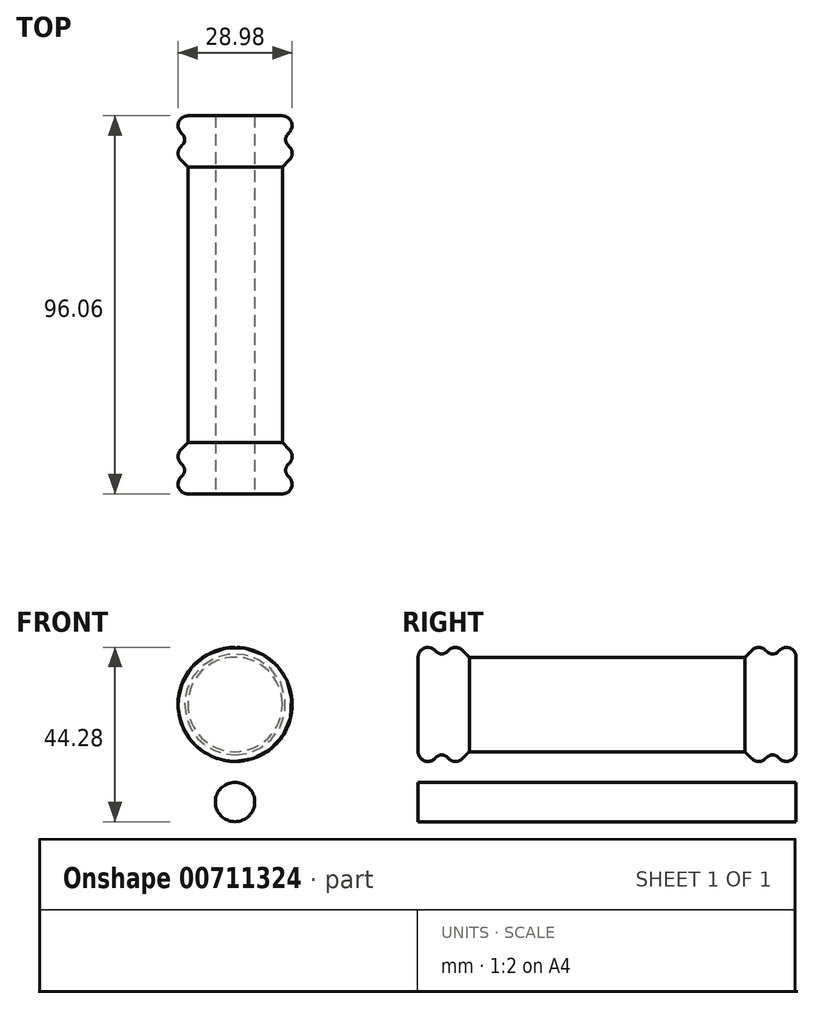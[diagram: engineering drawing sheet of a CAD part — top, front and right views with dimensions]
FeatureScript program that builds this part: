
annotation { "Feature Type Name" : "Feature", "Feature Type Description" : "" }
export const myFeature = defineFeature(function(context is Context, id is Id, definition is map)
    precondition{}
    {
        {
            var Q0;
            Q0=qCreatedBy(makeId("Right.planeOp"),FACE);
            var sketch = newSketch(context, id + "F0", { "sketchPlane" : qUnion([Q0])});
            skLineSegment(sketch, "E0", {"start": v(-48.03, 0) * mm, "end": v(-48.03, 12) * mm});
            skLineSegment(sketch, "E1", {"start": v(-43.79, 13.76) * mm, "end": v(-42.03, 12) * mm});
            skLineSegment(sketch, "E2", {"start": v(-42.03, 12) * mm, "end": v(-40.27, 13.76) * mm});
            skLineSegment(sketch, "E3", {"start": v(-36.76, 13.76) * mm, "end": v(-35, 12) * mm});
            skLineSegment(sketch, "E4", {"start": v(-48.03, 0) * mm, "end": v(48.03, 0) * mm});
            skLineSegment(sketch, "E5", {"start": v(-35, 12) * mm, "end": v(35, 12) * mm});
            skArc(sketch, "E6", {"start": v(-43.79, 13.76) * mm, "mid": v(-46.5, 14.3) * mm, "end": v(-48.03, 12) * mm});
            skArc(sketch, "E7", {"start": v(-36.76, 13.76) * mm, "mid": v(-38.51, 14.49) * mm, "end": v(-40.27, 13.76) * mm});
            skArc(sketch, "E8.MirrorCS", {"start": v(36.76, 13.76) * mm, "mid": v(38.51, 14.49) * mm, "end": v(40.27, 13.76) * mm});
            skLineSegment(sketch, "E9.MirrorCS", {"start": v(36.76, 13.76) * mm, "end": v(35, 12) * mm});
            skLineSegment(sketch, "E10.MirrorCS", {"start": v(42.03, 12) * mm, "end": v(40.27, 13.76) * mm});
            skLineSegment(sketch, "E11.MirrorCS", {"start": v(48.03, 0) * mm, "end": v(48.03, 12) * mm});
            skLineSegment(sketch, "E12.MirrorCS", {"start": v(43.79, 13.76) * mm, "end": v(42.03, 12) * mm});
            skArc(sketch, "E13.MirrorCS", {"start": v(43.79, 13.76) * mm, "mid": v(46.5, 14.3) * mm, "end": v(48.03, 12) * mm});
            skLineSegment(sketch, "E14.bottom", {"start": v(-48.03, -19.79) * mm, "end": v(48.03, -19.79) * mm});
            skLineSegment(sketch, "E14.top", {"start": v(-48.03, -24.79) * mm, "end": v(48.03, -24.79) * mm});
            skLineSegment(sketch, "E14.left", {"start": v(-48.03, -19.79) * mm, "end": v(-48.03, -24.79) * mm});
            skLineSegment(sketch, "E14.right", {"start": v(48.03, -19.79) * mm, "end": v(48.03, -24.79) * mm});
            skSolve(sketch);
        }
        {
            var Q0;
            Q0=makeQuery(id+"F0.imprint","IMPRINT",FACE,{"disambiguationData":[TD([[makeQuery(id+"F0.imprint","IMPRINT",EDGE,{"derivedFrom":sQuery(id+"F0.wireOp",EDGE,"E0")}),-1.0]])]});
            var Q1;
            Q1=sQuery(id+"F0.wireOp",EDGE,"E4");
            revolve(context, id + "F1", {"surfaceOperationType" : NewSurfaceOperationType.NEW, "entities" : qUnion([Q0]), "axis" : qUnion([Q1]), "revolveType" : RevolveType.FULL});
        }
        {
            var Q0;
            Q0=makeQuery(id+"F1.opRevolve","SWEPT_EDGE",EDGE,{"disambiguationData":[OSD([sQuery(id+"F0.wireOp",EDGE,"E1"),sQuery(id+"F0.wireOp",EDGE,"E2")])]});
            var Q1;
            Q1=makeQuery(id+"F1.opRevolve","SWEPT_EDGE",EDGE,{"disambiguationData":[OSD([sQuery(id+"F0.wireOp",EDGE,"E10.MirrorCS"),sQuery(id+"F0.wireOp",EDGE,"E12.MirrorCS")])]});
            fillet(context, id + "F2", {"entities" : qUnion([Q0, Q1]), "radius" : 2 * mm, "tangentPropagation" : true, "allowEdgeOverflow" : false});
        }
        {
            var Q0;
            Q0=makeQuery(id+"F0.imprint","IMPRINT",FACE,{"disambiguationData":[TD([[makeQuery(id+"F0.imprint","IMPRINT",EDGE,{"derivedFrom":sQuery(id+"F0.wireOp",EDGE,"E14.bottom")}),-1.0]])]});
            var Q1;
            Q1=sQuery(id+"F0.wireOp",EDGE,"E14.top");
            revolve(context, id + "F3", {"surfaceOperationType" : NewSurfaceOperationType.NEW, "entities" : qUnion([Q0]), "axis" : qUnion([Q1]), "revolveType" : RevolveType.FULL});
        }
    });
